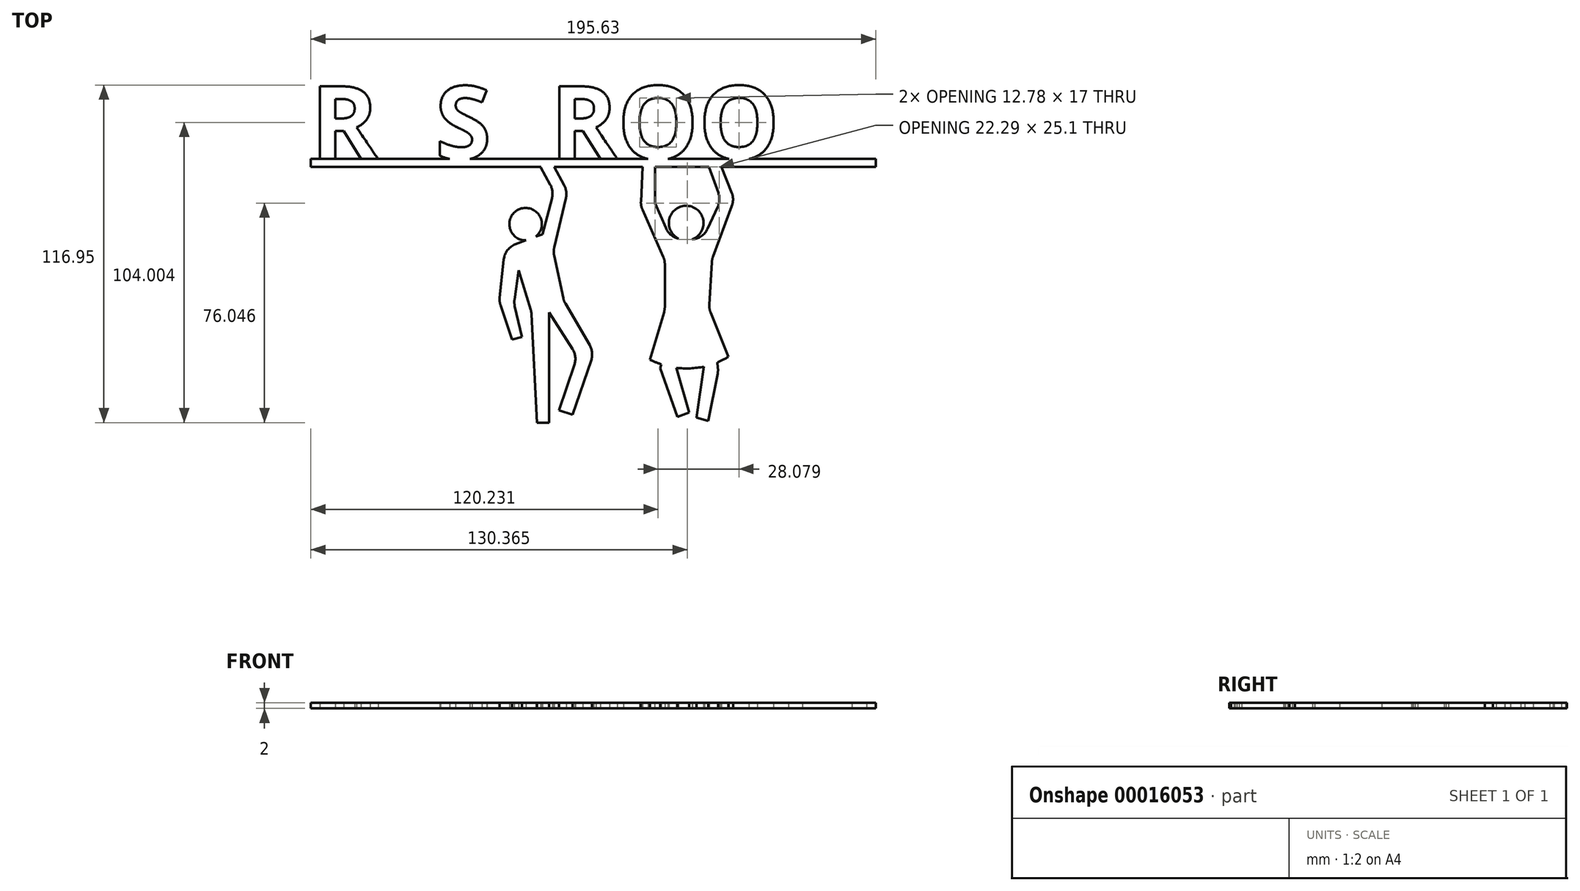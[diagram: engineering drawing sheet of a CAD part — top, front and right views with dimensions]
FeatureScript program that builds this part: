
annotation { "Feature Type Name" : "Feature", "Feature Type Description" : "" }
export const myFeature = defineFeature(function(context is Context, id is Id, definition is map)
    precondition{}
    {
        {
            var Q0;
            Q0=qCreatedBy(makeId("Top.planeOp"),FACE);
            var sketch = newSketch(context, id + "F0", { "sketchPlane" : qUnion([Q0])});
            skText(sketch, "E0", { "text": "RESTROOM", "fontName": "OpenSans-Bold.ttf"});
            skLineSegment(sketch, "E1.bottom", {"start": v(-30.47, -29.57) * mm, "end": v(165.16, -29.57) * mm});
            skLineSegment(sketch, "E1.top", {"start": v(-30.47, -32.35) * mm, "end": v(165.16, -32.35) * mm});
            skLineSegment(sketch, "E1.left", {"start": v(-30.47, -29.57) * mm, "end": v(-30.47, -32.35) * mm});
            skLineSegment(sketch, "E1.right", {"start": v(165.16, -29.57) * mm, "end": v(165.16, -32.35) * mm});
            const initialGuessF0  = {"E0": [-0.03047, -0.02957, 1, 0, 0.0254]};
            skSetInitialGuess(sketch, initialGuessF0);
            skSolve(sketch);
        }
        {
            var Q0;
            {var subQ1=sQuery(id+"F0.wireOp",EDGE,"E0.sketch_text.stroke-88");var subQ3=sQuery(id+"F0.wireOp",EDGE,"E0.sketch_text.stroke-87");var subQ5=makeQuery(id+"F0.imprint","INTERSECT",VERTEX,{"derivedFrom":[subQ3,subQ1]});Q0=makeQuery(id+"F0.imprint","IMPRINT",FACE,{"disambiguationData":[TD([[makeQuery(id+"F0.imprint","IMPRINT",EDGE,{"disambiguationData":[TD([[subQ5,1.0]])],"derivedFrom":subQ3}),-1.0]])]});}
            var Q1;
            {var subQ1=sQuery(id+"F0.wireOp",EDGE,"E0.sketch_text.stroke-102");var subQ3=sQuery(id+"F0.wireOp",EDGE,"E0.sketch_text.stroke-101");var subQ5=makeQuery(id+"F0.imprint","INTERSECT",VERTEX,{"derivedFrom":[subQ3,subQ1]});Q1=makeQuery(id+"F0.imprint","IMPRINT",FACE,{"disambiguationData":[TD([[makeQuery(id+"F0.imprint","IMPRINT",EDGE,{"disambiguationData":[TD([[subQ5,1.0]])],"derivedFrom":subQ3}),-1.0]])]});}
            var Q2;
            {var subQ6=sQuery(id+"F0.wireOp",EDGE,"E0.sketch_text.stroke-100");Q2=makeQuery(id+"F0.imprint","IMPRINT",FACE,{"disambiguationData":[TD([[makeQuery(id+"F0.imprint","IMPRINT",EDGE,{"derivedFrom":subQ6}),-1.0]])]});}
            var Q3;
            Q3=makeQuery(id+"F0.imprint","IMPRINT",FACE,{"disambiguationData":[TD([[makeQuery(id+"F0.imprint","IMPRINT",EDGE,{"derivedFrom":sQuery(id+"F0.wireOp",EDGE,"E1.top")}),1.0]])]});
            var Q4;
            {var subQ4=sQuery(id+"F0.wireOp",EDGE,"E0.sketch_text.stroke-114");Q4=makeQuery(id+"F0.imprint","IMPRINT",FACE,{"disambiguationData":[TD([[makeQuery(id+"F0.imprint","IMPRINT",EDGE,{"derivedFrom":subQ4}),-1.0]])]});}
            var Q5;
            {var subQ6=sQuery(id+"F0.wireOp",EDGE,"E0.sketch_text.stroke-86");Q5=makeQuery(id+"F0.imprint","IMPRINT",FACE,{"disambiguationData":[TD([[makeQuery(id+"F0.imprint","IMPRINT",EDGE,{"derivedFrom":subQ6}),-1.0]])]});}
            var Q6;
            Q6=makeQuery(id+"F0.imprint","IMPRINT",FACE,{"disambiguationData":[TD([[makeQuery(id+"F0.imprint","IMPRINT",EDGE,{"derivedFrom":sQuery(id+"F0.wireOp",EDGE,"E0.sketch_text.stroke-67")}),-1.0]])]});
            var Q7;
            {var subQ2=sQuery(id+"F0.wireOp",EDGE,"E0.sketch_text.stroke-60");Q7=makeQuery(id+"F0.imprint","IMPRINT",FACE,{"disambiguationData":[TD([[makeQuery(id+"F0.imprint","IMPRINT",EDGE,{"derivedFrom":subQ2}),-1.0]])]});}
            var Q8;
            {var subQ0=sQuery(id+"F0.wireOp",EDGE,"E0.sketch_text.stroke-33");var subQ3=sQuery(id+"F0.wireOp",EDGE,"E0.sketch_text.stroke-32");var subQ4=makeQuery(id+"F0.imprint","INTERSECT",VERTEX,{"derivedFrom":[subQ3,subQ0]});Q8=makeQuery(id+"F0.imprint","IMPRINT",FACE,{"disambiguationData":[TD([[makeQuery(id+"F0.imprint","IMPRINT",EDGE,{"disambiguationData":[TD([[subQ4,1.0]])],"derivedFrom":subQ3}),-1.0]])]});}
            var Q9;
            {var subQ5=sQuery(id+"F0.wireOp",EDGE,"E0.sketch_text.stroke-31");Q9=makeQuery(id+"F0.imprint","IMPRINT",FACE,{"disambiguationData":[TD([[makeQuery(id+"F0.imprint","IMPRINT",EDGE,{"derivedFrom":subQ5}),-1.0]])]});}
            var Q10;
            Q10=makeQuery(id+"F0.imprint","IMPRINT",FACE,{"disambiguationData":[TD([[makeQuery(id+"F0.imprint","IMPRINT",EDGE,{"derivedFrom":sQuery(id+"F0.wireOp",EDGE,"E0.sketch_text.stroke-0")}),-1.0]])]});
            var Q11;
            {var subQ2=sQuery(id+"F0.wireOp",EDGE,"E0.sketch_text.stroke-20");Q11=makeQuery(id+"F0.imprint","IMPRINT",FACE,{"disambiguationData":[TD([[makeQuery(id+"F0.imprint","IMPRINT",EDGE,{"derivedFrom":subQ2}),-1.0]])]});}
            extrude(context, id + "F1", {"entities" : qUnion([Q0, Q1, Q2, Q3, Q4, Q5, Q6, Q7, Q8, Q9, Q10, Q11]), "depth" : 2 * mm});
        }
        {
            var Q0;
            Q0=qCreatedBy(makeId("Top.planeOp"),FACE);
            var sketch = newSketch(context, id + "F2", { "sketchPlane" : qUnion([Q0])});
            skCircle(sketch, "E2", {"center": v(43.92, -52.15) * mm, "radius": 5.62 * mm});
            skLineSegment(sketch, "E3", {"start": v(40.43, -59.12) * mm, "end": v(49.76, -55.62) * mm});
            skLineSegment(sketch, "E4", {"start": v(49.76, -55.62) * mm, "end": v(53.04, -43.18) * mm});
            skLineSegment(sketch, "E5", {"start": v(52.5, -38.55) * mm, "end": v(49.17, -32.39) * mm});
            skLineSegment(sketch, "E6", {"start": v(49.17, -32.39) * mm, "end": v(52.83, -30.42) * mm});
            skLineSegment(sketch, "E7", {"start": v(52.83, -30.42) * mm, "end": v(57.28, -38.68) * mm});
            skLineSegment(sketch, "E8", {"start": v(57.87, -43.15) * mm, "end": v(53.83, -60.28) * mm});
            skLineSegment(sketch, "E9", {"start": v(53.8, -63.08) * mm, "end": v(56.98, -77.83) * mm});
            skLineSegment(sketch, "E10", {"start": v(57.7, -79.7) * mm, "end": v(66.1, -94.08) * mm});
            skLineSegment(sketch, "E11", {"start": v(66.62, -99.32) * mm, "end": v(60.22, -118.21) * mm});
            skLineSegment(sketch, "E12", {"start": v(60.22, -118.21) * mm, "end": v(55.49, -116.6) * mm});
            skLineSegment(sketch, "E13", {"start": v(55.49, -116.6) * mm, "end": v(60.81, -100.89) * mm});
            skLineSegment(sketch, "E14", {"start": v(60.16, -95.44) * mm, "end": v(52.04, -82.68) * mm});
            skLineSegment(sketch, "E15", {"start": v(52.04, -82.68) * mm, "end": v(52.04, -120.94) * mm});
            skLineSegment(sketch, "E16", {"start": v(52.04, -120.94) * mm, "end": v(47.85, -120.94) * mm});
            skLineSegment(sketch, "E17", {"start": v(47.85, -120.94) * mm, "end": v(45.96, -83.35) * mm});
            skLineSegment(sketch, "E18", {"start": v(45.7, -81.83) * mm, "end": v(41.54, -68.1) * mm});
            skLineSegment(sketch, "E19", {"start": v(41.54, -68.1) * mm, "end": v(40.08, -78.23) * mm});
            skLineSegment(sketch, "E20", {"start": v(40.17, -80.55) * mm, "end": v(42.63, -91.3) * mm});
            skLineSegment(sketch, "E21", {"start": v(42.63, -91.3) * mm, "end": v(39.18, -92.09) * mm});
            skLineSegment(sketch, "E22", {"start": v(39.18, -92.09) * mm, "end": v(35.26, -80.33) * mm});
            skLineSegment(sketch, "E23", {"start": v(34.97, -77.66) * mm, "end": v(36.34, -64.41) * mm});
            skCircle(sketch, "E24", {"center": v(99.54, -51.8) * mm, "radius": 6 * mm});
            skLineSegment(sketch, "E25", {"start": v(98.08, -57.34) * mm, "end": v(100.9, -57.45) * mm});
            skLineSegment(sketch, "E26", {"start": v(106.91, -53.79) * mm, "end": v(110.45, -46.19) * mm});
            skLineSegment(sketch, "E27", {"start": v(110.67, -41.35) * mm, "end": v(107.13, -31.55) * mm});
            skLineSegment(sketch, "E28", {"start": v(107.13, -31.55) * mm, "end": v(110.9, -30.2) * mm});
            skLineSegment(sketch, "E29", {"start": v(110.9, -30.2) * mm, "end": v(115.3, -41.29) * mm});
            skLineSegment(sketch, "E30", {"start": v(115.36, -45.84) * mm, "end": v(108.81, -63.48) * mm});
            skLineSegment(sketch, "E31", {"start": v(108.42, -65.32) * mm, "end": v(107.55, -80.08) * mm});
            skLineSegment(sketch, "E32", {"start": v(108, -82.8) * mm, "end": v(114.1, -98.15) * mm});
            skLineSegment(sketch, "E33", {"start": v(92.51, -53.53) * mm, "end": v(88.75, -44.91) * mm});
            skLineSegment(sketch, "E34", {"start": v(88.75, -44.91) * mm, "end": v(88.75, -31.37) * mm});
            skLineSegment(sketch, "E35", {"start": v(88.75, -31.37) * mm, "end": v(84.46, -31.37) * mm});
            skLineSegment(sketch, "E36", {"start": v(84.46, -31.37) * mm, "end": v(83.86, -44.34) * mm});
            skLineSegment(sketch, "E37", {"start": v(84.4, -47.2) * mm, "end": v(91.6, -63.49) * mm});
            skLineSegment(sketch, "E38", {"start": v(92.14, -66.05) * mm, "end": v(92.14, -80.77) * mm});
            skLineSegment(sketch, "E39", {"start": v(91.87, -82.59) * mm, "end": v(86.95, -99.08) * mm});
            skArc(sketch, "E40", {"start": v(86.95, -99.08) * mm, "mid": v(100.65, -102.12) * mm, "end": v(114.1, -98.15) * mm});
            skLineSegment(sketch, "E41", {"start": v(90.87, -100.72) * mm, "end": v(90.5, -102.1) * mm});
            skLineSegment(sketch, "E42", {"start": v(90.5, -102.1) * mm, "end": v(96.44, -118.92) * mm});
            skLineSegment(sketch, "E43", {"start": v(96.44, -118.92) * mm, "end": v(100.6, -117.45) * mm});
            skLineSegment(sketch, "E44", {"start": v(100.6, -117.45) * mm, "end": v(96.18, -101.92) * mm});
            skLineSegment(sketch, "E45", {"start": v(105.66, -101.5) * mm, "end": v(103.04, -119.23) * mm});
            skLineSegment(sketch, "E46", {"start": v(103.04, -119.23) * mm, "end": v(107.21, -120.3) * mm});
            skLineSegment(sketch, "E47", {"start": v(107.21, -120.3) * mm, "end": v(110.43, -103.9) * mm});
            skLineSegment(sketch, "E48", {"start": v(110.5, -101.95) * mm, "end": v(110.29, -100.06) * mm});
            skPoint(sketch, "E49.visualSharp", {"position": v(83.8, -45.83) * mm});
            skArc(sketch, "E49.filletArc", {"start": v(83.86, -44.34) * mm, "mid": v(83.97, -45.8) * mm, "end": v(84.4, -47.2) * mm});
            skPoint(sketch, "E50.visualSharp", {"position": v(116.2, -43.55) * mm});
            skArc(sketch, "E50.filletArc", {"start": v(115.36, -45.84) * mm, "mid": v(115.75, -43.56) * mm, "end": v(115.3, -41.29) * mm});
            skPoint(sketch, "E51.visualSharp", {"position": v(111.55, -43.81) * mm});
            skArc(sketch, "E51.filletArc", {"start": v(110.45, -46.19) * mm, "mid": v(111.04, -43.8) * mm, "end": v(110.67, -41.35) * mm});
            skPoint(sketch, "E52.visualSharp", {"position": v(108.48, -64.37) * mm});
            skArc(sketch, "E52.filletArc", {"start": v(108.81, -63.48) * mm, "mid": v(108.55, -64.39) * mm, "end": v(108.42, -65.32) * mm});
            skPoint(sketch, "E53.visualSharp", {"position": v(105.13, -57.62) * mm});
            skArc(sketch, "E53.filletArc", {"start": v(100.9, -57.45) * mm, "mid": v(104.47, -56.53) * mm, "end": v(106.91, -53.79) * mm});
            skPoint(sketch, "E54.visualSharp", {"position": v(94.1, -57.19) * mm});
            skArc(sketch, "E54.filletArc", {"start": v(92.51, -53.53) * mm, "mid": v(94.75, -56.24) * mm, "end": v(98.08, -57.34) * mm});
            skPoint(sketch, "E55.visualSharp", {"position": v(92.14, -64.71) * mm});
            skArc(sketch, "E55.filletArc", {"start": v(92.14, -66.05) * mm, "mid": v(92, -64.74) * mm, "end": v(91.6, -63.49) * mm});
            skPoint(sketch, "E56.visualSharp", {"position": v(92.14, -81.7) * mm});
            skArc(sketch, "E56.filletArc", {"start": v(91.87, -82.59) * mm, "mid": v(92.07, -81.7) * mm, "end": v(92.14, -80.77) * mm});
            skPoint(sketch, "E57.visualSharp", {"position": v(107.47, -81.5) * mm});
            skArc(sketch, "E57.filletArc", {"start": v(107.55, -80.08) * mm, "mid": v(107.62, -81.47) * mm, "end": v(108, -82.8) * mm});
            skPoint(sketch, "E58.visualSharp", {"position": v(110.62, -102.93) * mm});
            skArc(sketch, "E58.filletArc", {"start": v(110.43, -103.9) * mm, "mid": v(110.54, -102.93) * mm, "end": v(110.5, -101.95) * mm});
            skPoint(sketch, "E59.visualSharp", {"position": v(67.55, -96.58) * mm});
            skArc(sketch, "E59.filletArc", {"start": v(66.62, -99.32) * mm, "mid": v(66.93, -96.65) * mm, "end": v(66.1, -94.08) * mm});
            skPoint(sketch, "E60.visualSharp", {"position": v(61.79, -98) * mm});
            skArc(sketch, "E60.filletArc", {"start": v(60.81, -100.89) * mm, "mid": v(61.1, -98.1) * mm, "end": v(60.16, -95.44) * mm});
            skPoint(sketch, "E61.visualSharp", {"position": v(45.92, -82.57) * mm});
            skArc(sketch, "E61.filletArc", {"start": v(45.96, -83.35) * mm, "mid": v(45.87, -82.58) * mm, "end": v(45.7, -81.83) * mm});
            skPoint(sketch, "E62.visualSharp", {"position": v(57.2, -78.82) * mm});
            skArc(sketch, "E62.filletArc", {"start": v(56.98, -77.83) * mm, "mid": v(57.27, -78.8) * mm, "end": v(57.7, -79.7) * mm});
            skPoint(sketch, "E63.visualSharp", {"position": v(53.5, -61.68) * mm});
            skArc(sketch, "E63.filletArc", {"start": v(53.83, -60.28) * mm, "mid": v(53.66, -61.68) * mm, "end": v(53.8, -63.08) * mm});
            skPoint(sketch, "E64.visualSharp", {"position": v(58.43, -40.8) * mm});
            skArc(sketch, "E64.filletArc", {"start": v(57.87, -43.15) * mm, "mid": v(57.99, -40.86) * mm, "end": v(57.28, -38.68) * mm});
            skPoint(sketch, "E65.visualSharp", {"position": v(53.68, -40.76) * mm});
            skArc(sketch, "E65.filletArc", {"start": v(53.04, -43.18) * mm, "mid": v(53.21, -40.81) * mm, "end": v(52.5, -38.55) * mm});
            skPoint(sketch, "E66.visualSharp", {"position": v(36.75, -60.5) * mm});
            skArc(sketch, "E66.filletArc", {"start": v(40.43, -59.12) * mm, "mid": v(37.63, -61.19) * mm, "end": v(36.34, -64.41) * mm});
            skPoint(sketch, "E67.visualSharp", {"position": v(34.83, -79.03) * mm});
            skArc(sketch, "E67.filletArc", {"start": v(34.97, -77.66) * mm, "mid": v(34.97, -79.01) * mm, "end": v(35.26, -80.33) * mm});
            skPoint(sketch, "E68.visualSharp", {"position": v(39.91, -79.4) * mm});
            skArc(sketch, "E68.filletArc", {"start": v(40.08, -78.23) * mm, "mid": v(40.02, -79.4) * mm, "end": v(40.17, -80.55) * mm});
            skSolve(sketch);
        }
        {
            var Q0;
            {var subQ0=sQuery(id+"F2.wireOp",EDGE,"E3");var subQ1=sQuery(id+"F2.wireOp",EDGE,"E2");var subQ3=makeQuery(id+"F2.imprint","INTERSECT",VERTEX,{"disambiguationData":[OD(0.0)],"derivedFrom":[subQ1,subQ0]});Q0=makeQuery(id+"F2.imprint","IMPRINT",FACE,{"disambiguationData":[TD([[makeQuery(id+"F2.imprint","IMPRINT",EDGE,{"disambiguationData":[TD([[subQ3,1.0]])],"derivedFrom":subQ1}),1.0]])]});}
            var Q1;
            {var subQ0=sQuery(id+"F2.wireOp",EDGE,"E3");var subQ1=sQuery(id+"F2.wireOp",EDGE,"E2");var subQ3=makeQuery(id+"F2.imprint","INTERSECT",VERTEX,{"disambiguationData":[OD(0.0)],"derivedFrom":[subQ1,subQ0]});Q1=makeQuery(id+"F2.imprint","IMPRINT",FACE,{"disambiguationData":[TD([[makeQuery(id+"F2.imprint","IMPRINT",EDGE,{"disambiguationData":[TD([[subQ3,-1.0]])],"derivedFrom":subQ1}),1.0]])]});}
            var Q2;
            {var subQ5=sQuery(id+"F2.wireOp",EDGE,"E4");Q2=makeQuery(id+"F2.imprint","IMPRINT",FACE,{"disambiguationData":[TD([[makeQuery(id+"F2.imprint","IMPRINT",EDGE,{"derivedFrom":subQ5}),-1.0]])]});}
            var Q3;
            {var subQ3=sQuery(id+"F2.wireOp",EDGE,"E25");Q3=makeQuery(id+"F2.imprint","IMPRINT",FACE,{"disambiguationData":[TD([[makeQuery(id+"F2.imprint","IMPRINT",EDGE,{"derivedFrom":subQ3}),1.0]])]});}
            var Q4;
            {var subQ3=sQuery(id+"F2.wireOp",EDGE,"E25");Q4=makeQuery(id+"F2.imprint","IMPRINT",FACE,{"disambiguationData":[TD([[makeQuery(id+"F2.imprint","IMPRINT",EDGE,{"derivedFrom":subQ3}),-1.0]])]});}
            var Q5;
            {var subQ6=sQuery(id+"F2.wireOp",EDGE,"E26");Q5=makeQuery(id+"F2.imprint","IMPRINT",FACE,{"disambiguationData":[TD([[makeQuery(id+"F2.imprint","IMPRINT",EDGE,{"derivedFrom":subQ6}),-1.0]])]});}
            var Q6;
            {var subQ1=sQuery(id+"F2.wireOp",EDGE,"E41");Q6=makeQuery(id+"F2.imprint","IMPRINT",FACE,{"disambiguationData":[TD([[makeQuery(id+"F2.imprint","IMPRINT",EDGE,{"derivedFrom":subQ1}),1.0]])]});}
            var Q7;
            {var subQ1=sQuery(id+"F2.wireOp",EDGE,"E45");Q7=makeQuery(id+"F2.imprint","IMPRINT",FACE,{"disambiguationData":[TD([[makeQuery(id+"F2.imprint","IMPRINT",EDGE,{"derivedFrom":subQ1}),1.0]])]});}
            extrude(context, id + "F3", {"entities" : qUnion([Q0, Q1, Q2, Q3, Q4, Q5, Q6, Q7]), "operationType" : NewBodyOperationType.ADD, "depth" : 2 * mm});
        }
    });
